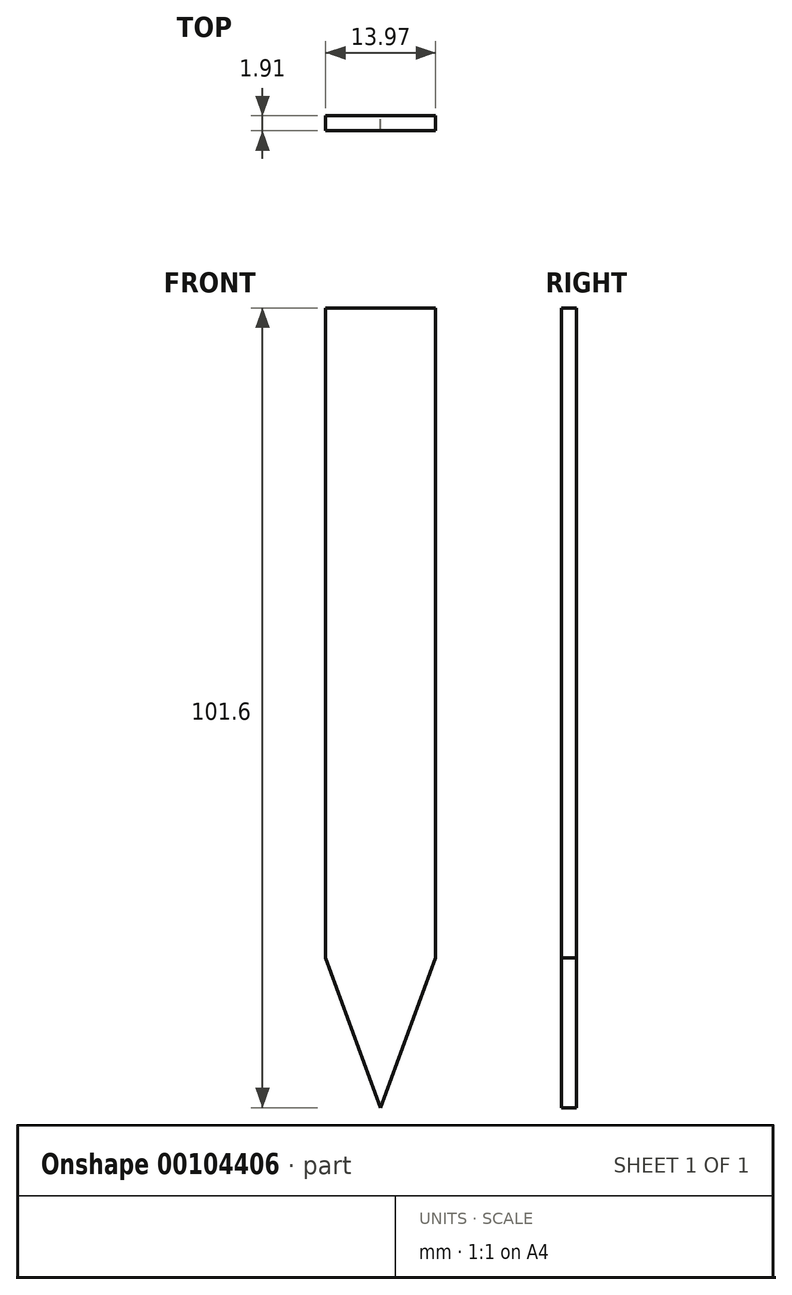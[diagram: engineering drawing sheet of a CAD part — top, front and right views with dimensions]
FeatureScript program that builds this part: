
annotation { "Feature Type Name" : "Feature", "Feature Type Description" : "" }
export const myFeature = defineFeature(function(context is Context, id is Id, definition is map)
    precondition{}
    {
        {
            var Q0;
            Q0=qCreatedBy(makeId("Front.planeOp"),FACE);
            var sketch = newSketch(context, id + "F0", { "sketchPlane" : qUnion([Q0])});
            skLineSegment(sketch, "E0", {"start": v(-9.71, 29.18) * mm, "end": v(-9.71, -53.37) * mm});
            skLineSegment(sketch, "E1", {"start": v(4.26, 29.18) * mm, "end": v(4.26, -53.37) * mm});
            skLineSegment(sketch, "E2", {"start": v(4.26, 29.18) * mm, "end": v(-9.71, 29.18) * mm});
            skLineSegment(sketch, "E3", {"start": v(-9.71, -53.37) * mm, "end": v(-2.73, -72.42) * mm});
            skLineSegment(sketch, "E4", {"start": v(-2.73, -72.42) * mm, "end": v(4.26, -53.37) * mm});
            skSolve(sketch);
        }
        {
            var Q0;
            Q0 = qSketchRegion(id + "F0", true);
            extrude(context, id + "F1", {"entities" : qUnion([Q0]), "depth" : 1.9 * mm});
        }
    });
